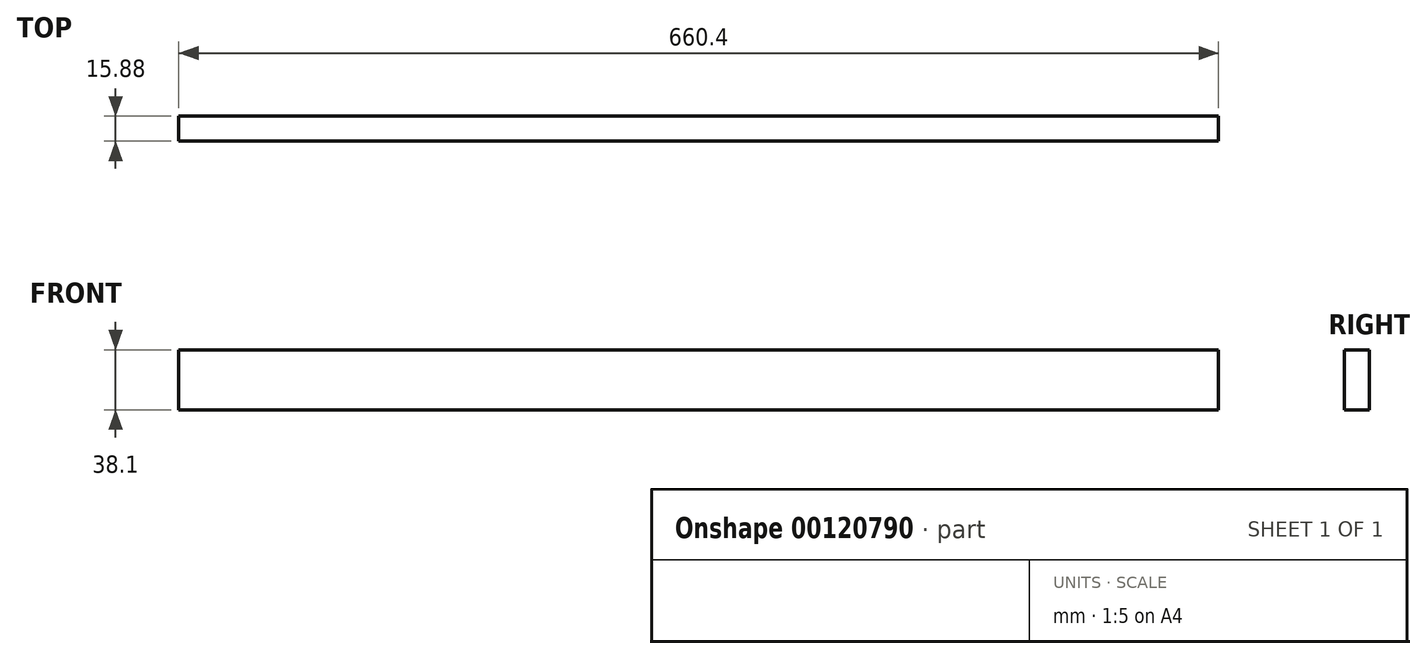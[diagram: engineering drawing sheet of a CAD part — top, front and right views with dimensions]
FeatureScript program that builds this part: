
annotation { "Feature Type Name" : "Feature", "Feature Type Description" : "" }
export const myFeature = defineFeature(function(context is Context, id is Id, definition is map)
    precondition{}
    {
        {
            var Q0;
            Q0=qCreatedBy(makeId("Front.planeOp"),FACE);
            var sketch = newSketch(context, id + "F0", { "sketchPlane" : qUnion([Q0])});
            skLineSegment(sketch, "E0.bottom", {"start": v(-330.2, 19.05) * mm, "end": v(330.2, 19.05) * mm});
            skLineSegment(sketch, "E0.top", {"start": v(-330.2, -19.05) * mm, "end": v(330.2, -19.05) * mm});
            skLineSegment(sketch, "E0.left", {"start": v(-330.2, 19.05) * mm, "end": v(-330.2, -19.05) * mm});
            skLineSegment(sketch, "E0.right", {"start": v(330.2, 19.05) * mm, "end": v(330.2, -19.05) * mm});
            skPoint(sketch, "E0.middle", {"position": v(0, 0) * mm});
            skSolve(sketch);
        }
        {
            var Q0;
            Q0=makeQuery(id+"F0.imprint","IMPRINT",FACE,{"disambiguationData":[TD([[makeQuery(id+"F0.imprint","IMPRINT",EDGE,{"derivedFrom":sQuery(id+"F0.wireOp",EDGE,"E0.bottom")}),-1.0]])]});
            extrude(context, id + "F1", {"entities" : qUnion([Q0]), "endBound" : BoundingType.SYMMETRIC, "depth" : 15.88 * mm});
        }
    });
